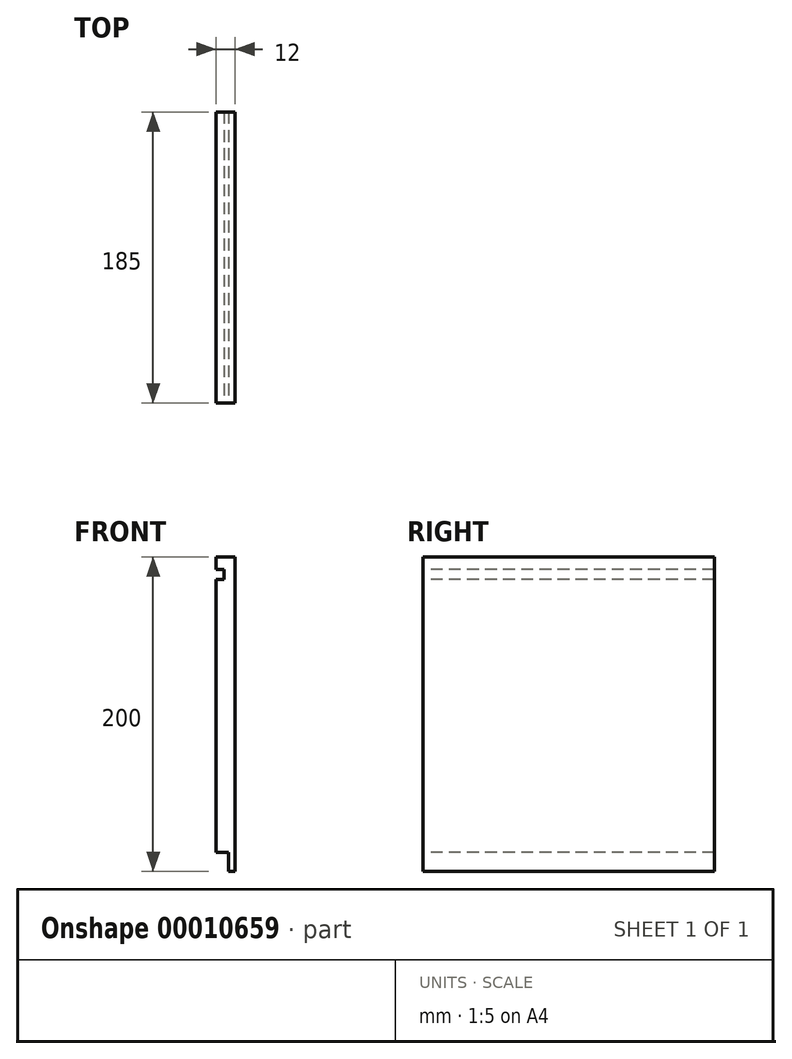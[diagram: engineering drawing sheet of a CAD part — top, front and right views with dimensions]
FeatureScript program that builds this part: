
annotation { "Feature Type Name" : "Feature", "Feature Type Description" : "" }
export const myFeature = defineFeature(function(context is Context, id is Id, definition is map)
    precondition{}
    {
        {
            var Q0;
            Q0=qCreatedBy(makeId("Right.planeOp"),FACE);
            var sketch = newSketch(context, id + "F0", { "sketchPlane" : qUnion([Q0])});
            skLineSegment(sketch, "E0.bottom", {"start": v(0, 0) * mm, "end": v(185, 0) * mm});
            skLineSegment(sketch, "E0.top", {"start": v(0, 200) * mm, "end": v(185, 200) * mm});
            skLineSegment(sketch, "E0.left", {"start": v(0, 0) * mm, "end": v(0, 200) * mm});
            skLineSegment(sketch, "E0.right", {"start": v(185, 0) * mm, "end": v(185, 200) * mm});
            skSolve(sketch);
        }
        {
            var Q0;
            Q0=makeQuery(id+"F0.imprint","IMPRINT",FACE,{"disambiguationData":[TD([[makeQuery(id+"F0.imprint","IMPRINT",EDGE,{"derivedFrom":sQuery(id+"F0.wireOp",EDGE,"E0.bottom")}),1.0]])]});
            extrude(context, id + "F1", {"entities" : qUnion([Q0]), "depth" : 12 * mm});
        }
        {
            var Q0;
            Q0=makeQuery(id+"F1.opExtrude","CAP_FACE",FACE,{"disambiguationData":[OSD([sQuery(id+"F0.wireOp",EDGE,"E0.bottom"),sQuery(id+"F0.wireOp",EDGE,"E0.top"),sQuery(id+"F0.wireOp",EDGE,"E0.left"),sQuery(id+"F0.wireOp",EDGE,"E0.right")])],"isStart":false});
            var sketch = newSketch(context, id + "F2", { "sketchPlane" : qUnion([Q0])});
            skLineSegment(sketch, "E1.bottom", {"start": v(0, 0) * mm, "end": v(185, 0) * mm});
            skLineSegment(sketch, "E1.top", {"start": v(0, 12.2) * mm, "end": v(185, 12.2) * mm});
            skLineSegment(sketch, "E1.left", {"start": v(0, 0) * mm, "end": v(0, 12.2) * mm});
            skLineSegment(sketch, "E1.right", {"start": v(185, 0) * mm, "end": v(185, 12.2) * mm});
            skSolve(sketch);
        }
        {
            var Q0;
            Q0=makeQuery(id+"F2.imprint","IMPRINT",FACE,{"disambiguationData":[TD([[makeQuery(id+"F2.imprint","IMPRINT",EDGE,{"derivedFrom":sQuery(id+"F2.wireOp",EDGE,"E1.bottom")}),1.0]])]});
            extrude(context, id + "F3", {"entities" : qUnion([Q0]), "operationType" : NewBodyOperationType.REMOVE, "oppositeDirection" : true, "depth" : 8 * mm});
        }
        {
            var Q0;
            Q0=makeQuery(id+"F1.opExtrude","SWEPT_BODY",BODY,{"disambiguationData":[OSD([sQuery(id+"F0.wireOp",EDGE,"E0.bottom"),sQuery(id+"F0.wireOp",EDGE,"E0.top"),sQuery(id+"F0.wireOp",EDGE,"E0.left"),sQuery(id+"F0.wireOp",EDGE,"E0.right")])]});
            var Q1;
            Q1=makeQuery(id+"F1.opExtrude","CAP_EDGE",EDGE,{"disambiguationData":[OSD([sQuery(id+"F0.wireOp",EDGE,"E0.left")])],"isStart":true});
            transform(context, id + "F4", {"entities" : qUnion([Q0]), "transformType" : TransformType.ROTATION, "transformAxis" : qUnion([Q1]), "angle" : 180 * degree, "makeCopy" : false});
        }
        {
            var Q0;
            Q0=makeQuery(id+"F1.opExtrude","CAP_FACE",FACE,{"disambiguationData":[OSD([sQuery(id+"F0.wireOp",EDGE,"E0.bottom"),sQuery(id+"F0.wireOp",EDGE,"E0.top"),sQuery(id+"F0.wireOp",EDGE,"E0.left"),sQuery(id+"F0.wireOp",EDGE,"E0.right")])],"isStart":false});
            var sketch = newSketch(context, id + "F5", { "sketchPlane" : qUnion([Q0])});
            skLineSegment(sketch, "E2.bottom", {"start": v(0, 192) * mm, "end": v(185, 192) * mm});
            skLineSegment(sketch, "E2.top", {"start": v(0, 185.5) * mm, "end": v(185, 185.5) * mm});
            skLineSegment(sketch, "E2.left", {"start": v(0, 192) * mm, "end": v(0, 185.5) * mm});
            skLineSegment(sketch, "E2.right", {"start": v(185, 192) * mm, "end": v(185, 185.5) * mm});
            skSolve(sketch);
        }
        {
            var Q0;
            Q0=makeQuery(id+"F5.imprint","IMPRINT",FACE,{"disambiguationData":[TD([[makeQuery(id+"F5.imprint","IMPRINT",EDGE,{"derivedFrom":sQuery(id+"F5.wireOp",EDGE,"E2.bottom")}),-1.0]])]});
            extrude(context, id + "F6", {"entities" : qUnion([Q0]), "operationType" : NewBodyOperationType.REMOVE, "oppositeDirection" : true, "depth" : 5 * mm});
        }
    });
